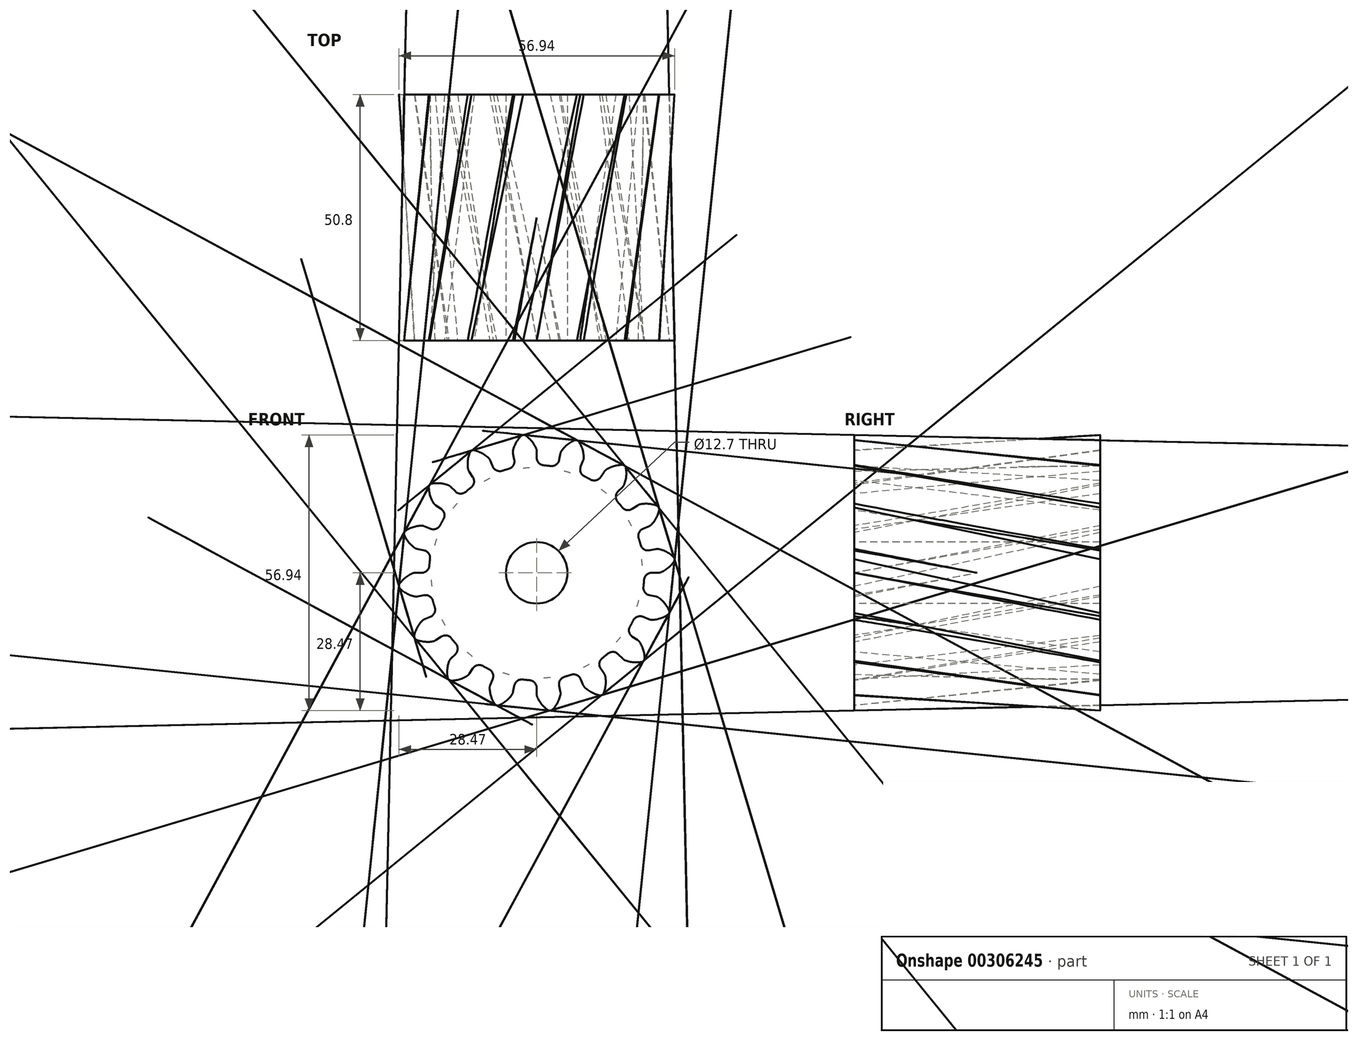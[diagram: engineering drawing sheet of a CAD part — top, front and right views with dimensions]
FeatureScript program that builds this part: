
annotation { "Feature Type Name" : "Feature", "Feature Type Description" : "" }
export const myFeature = defineFeature(function(context is Context, id is Id, definition is map)
    precondition{}
    {
        {
            var Q0;
            Q0=qCreatedBy(makeId("Front.planeOp"),FACE);
            var sketch = newSketch(context, id + "F0", { "sketchPlane" : qUnion([Q0])});
            skArc(sketch, "E0", {"start": v(-5.78, 21.46) * mm, "mid": v(-6.45, 21.27) * mm, "end": v(-7.12, 21.05) * mm});
            skArc(sketch, "E1.trimOffspring", {"start": v(-0.14, 25.74) * mm, "mid": v(-1.06, 27.2) * mm, "end": v(-2.34, 28.36) * mm});
            skLineSegment(sketch, "E2", {"start": v(-2.68, 28.45) * mm, "end": v(-2.8, 28.44) * mm});
            skLineSegment(sketch, "E3", {"start": v(0, 25.08) * mm, "end": v(0, 23.76) * mm});
            skLineSegment(sketch, "E4.MirrorCS", {"start": v(-4.9, 24.6) * mm, "end": v(-4.64, 23.3) * mm});
            skArc(sketch, "E5.MirrorCS", {"start": v(-4.88, 25.27) * mm, "mid": v(-4.27, 26.89) * mm, "end": v(-3.23, 28.28) * mm});
            skLineSegment(sketch, "E6.MirrorCS", {"start": v(-2.93, 28.43) * mm, "end": v(-2.8, 28.44) * mm});
            skPoint(sketch, "E7.visualSharp", {"position": v(-4.34, 21.8) * mm});
            skArc(sketch, "E7.filletArc", {"start": v(-5.78, 21.46) * mm, "mid": v(-4.84, 22.16) * mm, "end": v(-4.64, 23.3) * mm});
            skPoint(sketch, "E8.visualSharp", {"position": v(0, 22.23) * mm});
            skArc(sketch, "E8.filletArc", {"start": v(0, 23.76) * mm, "mid": v(0.43, 22.68) * mm, "end": v(1.48, 22.18) * mm});
            skPoint(sketch, "E9.visualSharp", {"position": v(-4.96, 24.91) * mm});
            skArc(sketch, "E9.filletArc", {"start": v(-4.88, 25.27) * mm, "mid": v(-4.92, 24.94) * mm, "end": v(-4.9, 24.6) * mm});
            skPoint(sketch, "E10.visualSharp", {"position": v(0, 25.4) * mm});
            skArc(sketch, "E10.filletArc", {"start": v(0, 25.08) * mm, "mid": v(-0.04, 25.42) * mm, "end": v(-0.14, 25.74) * mm});
            skPoint(sketch, "E11.visualSharp", {"position": v(-3.1, 28.4) * mm});
            skArc(sketch, "E11.filletArc", {"start": v(-2.93, 28.43) * mm, "mid": v(-3.1, 28.38) * mm, "end": v(-3.23, 28.28) * mm});
            skPoint(sketch, "E12.visualSharp", {"position": v(-2.5, 28.47) * mm});
            skArc(sketch, "E12.filletArc", {"start": v(-2.34, 28.36) * mm, "mid": v(-2.5, 28.44) * mm, "end": v(-2.68, 28.45) * mm});
            skPoint(sketch, "E13.1.0", {"position": v(-12.35, 18.48) * mm});
            skLineSegment(sketch, "E13.1.1", {"start": v(-9.6, 23.17) * mm, "end": v(-9.1, 21.95) * mm});
            skPoint(sketch, "E13.1.2", {"position": v(-13.2, 25.34) * mm});
            skArc(sketch, "E13.1.3", {"start": v(-14.18, 21.48) * mm, "mid": v(-14.23, 23.2) * mm, "end": v(-13.8, 24.89) * mm});
            skPoint(sketch, "E13.1.4", {"position": v(-13.74, 25.06) * mm});
            skPoint(sketch, "E13.1.5", {"position": v(-9.72, 23.47) * mm});
            skPoint(sketch, "E13.1.6", {"position": v(-14.11, 21.12) * mm});
            skPoint(sketch, "E13.1.7", {"position": v(-8.5, 20.53) * mm});
            skArc(sketch, "E13.1.8", {"start": v(-13.55, 17.62) * mm, "mid": v(-12.95, 18.62) * mm, "end": v(-13.2, 19.76) * mm});
            skArc(sketch, "E13.1.9", {"start": v(-9.98, 23.72) * mm, "mid": v(-11.4, 24.72) * mm, "end": v(-13.02, 25.3) * mm});
            skLineSegment(sketch, "E13.1.10", {"start": v(-13.94, 20.86) * mm, "end": v(-13.2, 19.76) * mm});
            skArc(sketch, "E13.1.11", {"start": v(-9.1, 21.95) * mm, "mid": v(-8.28, 21.11) * mm, "end": v(-7.12, 21.05) * mm});
            skArc(sketch, "E13.1.12", {"start": v(-14.18, 21.48) * mm, "mid": v(-14.1, 21.15) * mm, "end": v(-13.94, 20.86) * mm});
            skArc(sketch, "E13.1.13", {"start": v(-9.6, 23.17) * mm, "mid": v(-9.76, 23.47) * mm, "end": v(-9.98, 23.72) * mm});
            skArc(sketch, "E13.1.14", {"start": v(-13.58, 25.14) * mm, "mid": v(-13.72, 25.03) * mm, "end": v(-13.8, 24.89) * mm});
            skArc(sketch, "E13.1.15", {"start": v(-13.02, 25.3) * mm, "mid": v(-13.2, 25.31) * mm, "end": v(-13.36, 25.26) * mm});
            skLineSegment(sketch, "E13.1.16", {"start": v(-13.58, 25.14) * mm, "end": v(-13.47, 25.2) * mm});
            skLineSegment(sketch, "E13.1.17", {"start": v(-13.36, 25.26) * mm, "end": v(-13.47, 25.2) * mm});
            skPoint(sketch, "E13.2.0", {"position": v(-18.48, 12.35) * mm});
            skLineSegment(sketch, "E13.2.1", {"start": v(-17.74, 17.74) * mm, "end": v(-16.8, 16.8) * mm});
            skPoint(sketch, "E13.2.2", {"position": v(-21.9, 18.36) * mm});
            skArc(sketch, "E13.2.3", {"start": v(-21.32, 14.42) * mm, "mid": v(-22.03, 16) * mm, "end": v(-22.28, 17.7) * mm});
            skPoint(sketch, "E13.2.4", {"position": v(-22.28, 17.9) * mm});
            skPoint(sketch, "E13.2.5", {"position": v(-17.96, 17.96) * mm});
            skPoint(sketch, "E13.2.6", {"position": v(-21.12, 14.11) * mm});
            skPoint(sketch, "E13.2.7", {"position": v(-15.72, 15.72) * mm});
            skArc(sketch, "E13.2.8", {"start": v(-19.26, 11.09) * mm, "mid": v(-19.1, 12.24) * mm, "end": v(-19.76, 13.2) * mm});
            skArc(sketch, "E13.2.9", {"start": v(-18.3, 18.1) * mm, "mid": v(-19.99, 18.48) * mm, "end": v(-21.71, 18.4) * mm});
            skLineSegment(sketch, "E13.2.10", {"start": v(-20.86, 13.94) * mm, "end": v(-19.76, 13.2) * mm});
            skArc(sketch, "E13.2.11", {"start": v(-16.8, 16.8) * mm, "mid": v(-15.73, 16.34) * mm, "end": v(-14.63, 16.73) * mm});
            skArc(sketch, "E13.2.12", {"start": v(-21.32, 14.42) * mm, "mid": v(-21.11, 14.15) * mm, "end": v(-20.86, 13.94) * mm});
            skArc(sketch, "E13.2.13", {"start": v(-17.74, 17.74) * mm, "mid": v(-18, 17.95) * mm, "end": v(-18.3, 18.1) * mm});
            skArc(sketch, "E13.2.14", {"start": v(-22.17, 18.03) * mm, "mid": v(-22.25, 17.88) * mm, "end": v(-22.28, 17.7) * mm});
            skArc(sketch, "E13.2.15", {"start": v(-21.71, 18.4) * mm, "mid": v(-21.88, 18.34) * mm, "end": v(-22, 18.23) * mm});
            skLineSegment(sketch, "E13.2.16", {"start": v(-22.17, 18.03) * mm, "end": v(-22.1, 18.13) * mm});
            skLineSegment(sketch, "E13.2.17", {"start": v(-22, 18.23) * mm, "end": v(-22.1, 18.13) * mm});
            skLineSegment(sketch, "E14.1.3.0", {"start": v(-23.17, 9.6) * mm, "end": v(-21.95, 9.1) * mm});
            skPoint(sketch, "E14.4.3.0", {"position": v(-27.25, 8.59) * mm});
            skArc(sketch, "E14.5.3.0", {"start": v(-25.22, 5.16) * mm, "mid": v(-26.47, 6.35) * mm, "end": v(-27.36, 7.83) * mm});
            skPoint(sketch, "E14.9.3.0", {"position": v(-27.43, 8) * mm});
            skPoint(sketch, "E14.10.3.0", {"position": v(-23.47, 9.72) * mm});
            skPoint(sketch, "E14.11.3.0", {"position": v(-24.91, 4.96) * mm});
            skPoint(sketch, "E14.12.3.0", {"position": v(-20.53, 8.5) * mm});
            skArc(sketch, "E14.13.3.0", {"start": v(-22.04, 2.87) * mm, "mid": v(-22.32, 4) * mm, "end": v(-23.3, 4.64) * mm});
            skPoint(sketch, "E14.15.3.0", {"position": v(-21.8, 4.34) * mm});
            skArc(sketch, "E14.17.3.0", {"start": v(-23.83, 9.72) * mm, "mid": v(-25.54, 9.43) * mm, "end": v(-27.1, 8.69) * mm});
            skLineSegment(sketch, "E14.21.3.0", {"start": v(-24.6, 4.9) * mm, "end": v(-23.3, 4.64) * mm});
            skArc(sketch, "E14.24.3.0", {"start": v(-21.95, 9.1) * mm, "mid": v(-20.79, 9.07) * mm, "end": v(-19.92, 9.86) * mm});
            skArc(sketch, "E14.28.3.0", {"start": v(-25.22, 5.16) * mm, "mid": v(-24.92, 5) * mm, "end": v(-24.6, 4.9) * mm});
            skArc(sketch, "E14.32.3.0", {"start": v(-23.17, 9.6) * mm, "mid": v(-23.5, 9.7) * mm, "end": v(-23.83, 9.72) * mm});
            skArc(sketch, "E14.36.3.0", {"start": v(-27.38, 8.17) * mm, "mid": v(-27.4, 8) * mm, "end": v(-27.36, 7.83) * mm});
            skArc(sketch, "E14.40.3.0", {"start": v(-27.1, 8.69) * mm, "mid": v(-27.23, 8.57) * mm, "end": v(-27.3, 8.42) * mm});
            skLineSegment(sketch, "E14.44.3.0", {"start": v(-27.38, 8.17) * mm, "end": v(-27.35, 8.3) * mm});
            skLineSegment(sketch, "E14.47.3.0", {"start": v(-27.3, 8.42) * mm, "end": v(-27.35, 8.3) * mm});
            skLineSegment(sketch, "E14.1.4.0", {"start": v(-25.08, 0) * mm, "end": v(-23.76, 0) * mm});
            skPoint(sketch, "E14.4.4.0", {"position": v(-28.47, -2.5) * mm});
            skArc(sketch, "E14.5.4.0", {"start": v(-25.27, -4.88) * mm, "mid": v(-26.89, -4.27) * mm, "end": v(-28.28, -3.23) * mm});
            skPoint(sketch, "E14.9.4.0", {"position": v(-28.4, -3.1) * mm});
            skPoint(sketch, "E14.10.4.0", {"position": v(-25.4, 0) * mm});
            skPoint(sketch, "E14.11.4.0", {"position": v(-24.91, -4.96) * mm});
            skPoint(sketch, "E14.12.4.0", {"position": v(-22.23, 0) * mm});
            skArc(sketch, "E14.13.4.0", {"start": v(-21.46, -5.78) * mm, "mid": v(-22.16, -4.84) * mm, "end": v(-23.3, -4.64) * mm});
            skPoint(sketch, "E14.15.4.0", {"position": v(-21.8, -4.34) * mm});
            skArc(sketch, "E14.17.4.0", {"start": v(-25.74, -0.14) * mm, "mid": v(-27.2, -1.06) * mm, "end": v(-28.36, -2.34) * mm});
            skLineSegment(sketch, "E14.21.4.0", {"start": v(-24.6, -4.9) * mm, "end": v(-23.3, -4.64) * mm});
            skArc(sketch, "E14.24.4.0", {"start": v(-23.76, 0) * mm, "mid": v(-22.68, 0.43) * mm, "end": v(-22.18, 1.48) * mm});
            skArc(sketch, "E14.28.4.0", {"start": v(-25.27, -4.88) * mm, "mid": v(-24.94, -4.92) * mm, "end": v(-24.6, -4.9) * mm});
            skArc(sketch, "E14.32.4.0", {"start": v(-25.08, 0) * mm, "mid": v(-25.42, -0.04) * mm, "end": v(-25.74, -0.14) * mm});
            skArc(sketch, "E14.36.4.0", {"start": v(-28.43, -2.93) * mm, "mid": v(-28.38, -3.1) * mm, "end": v(-28.28, -3.23) * mm});
            skArc(sketch, "E14.40.4.0", {"start": v(-28.36, -2.34) * mm, "mid": v(-28.44, -2.5) * mm, "end": v(-28.45, -2.68) * mm});
            skLineSegment(sketch, "E14.44.4.0", {"start": v(-28.43, -2.93) * mm, "end": v(-28.44, -2.8) * mm});
            skLineSegment(sketch, "E14.47.4.0", {"start": v(-28.45, -2.68) * mm, "end": v(-28.44, -2.8) * mm});
            skLineSegment(sketch, "E14.1.5.0", {"start": v(-23.17, -9.6) * mm, "end": v(-21.95, -9.1) * mm});
            skPoint(sketch, "E14.4.5.0", {"position": v(-25.34, -13.2) * mm});
            skArc(sketch, "E14.5.5.0", {"start": v(-21.48, -14.18) * mm, "mid": v(-23.2, -14.23) * mm, "end": v(-24.89, -13.8) * mm});
            skPoint(sketch, "E14.9.5.0", {"position": v(-25.06, -13.74) * mm});
            skPoint(sketch, "E14.10.5.0", {"position": v(-23.47, -9.72) * mm});
            skPoint(sketch, "E14.11.5.0", {"position": v(-21.12, -14.11) * mm});
            skPoint(sketch, "E14.12.5.0", {"position": v(-20.53, -8.5) * mm});
            skArc(sketch, "E14.13.5.0", {"start": v(-17.62, -13.55) * mm, "mid": v(-18.62, -12.95) * mm, "end": v(-19.76, -13.2) * mm});
            skPoint(sketch, "E14.15.5.0", {"position": v(-18.48, -12.35) * mm});
            skArc(sketch, "E14.17.5.0", {"start": v(-23.72, -9.98) * mm, "mid": v(-24.72, -11.4) * mm, "end": v(-25.3, -13.02) * mm});
            skLineSegment(sketch, "E14.21.5.0", {"start": v(-20.86, -13.94) * mm, "end": v(-19.76, -13.2) * mm});
            skArc(sketch, "E14.24.5.0", {"start": v(-21.95, -9.1) * mm, "mid": v(-21.11, -8.28) * mm, "end": v(-21.05, -7.12) * mm});
            skArc(sketch, "E14.28.5.0", {"start": v(-21.48, -14.18) * mm, "mid": v(-21.15, -14.1) * mm, "end": v(-20.86, -13.94) * mm});
            skArc(sketch, "E14.32.5.0", {"start": v(-23.17, -9.6) * mm, "mid": v(-23.47, -9.76) * mm, "end": v(-23.72, -9.98) * mm});
            skArc(sketch, "E14.36.5.0", {"start": v(-25.14, -13.58) * mm, "mid": v(-25.03, -13.72) * mm, "end": v(-24.89, -13.8) * mm});
            skArc(sketch, "E14.40.5.0", {"start": v(-25.3, -13.02) * mm, "mid": v(-25.31, -13.2) * mm, "end": v(-25.26, -13.36) * mm});
            skLineSegment(sketch, "E14.44.5.0", {"start": v(-25.14, -13.58) * mm, "end": v(-25.2, -13.47) * mm});
            skLineSegment(sketch, "E14.47.5.0", {"start": v(-25.26, -13.36) * mm, "end": v(-25.2, -13.47) * mm});
            skLineSegment(sketch, "E14.1.6.0", {"start": v(-17.74, -17.74) * mm, "end": v(-16.8, -16.8) * mm});
            skPoint(sketch, "E14.4.6.0", {"position": v(-18.36, -21.9) * mm});
            skArc(sketch, "E14.5.6.0", {"start": v(-14.42, -21.32) * mm, "mid": v(-16, -22.03) * mm, "end": v(-17.7, -22.28) * mm});
            skPoint(sketch, "E14.9.6.0", {"position": v(-17.9, -22.28) * mm});
            skPoint(sketch, "E14.10.6.0", {"position": v(-17.96, -17.96) * mm});
            skPoint(sketch, "E14.11.6.0", {"position": v(-14.11, -21.12) * mm});
            skPoint(sketch, "E14.12.6.0", {"position": v(-15.72, -15.72) * mm});
            skArc(sketch, "E14.13.6.0", {"start": v(-11.09, -19.26) * mm, "mid": v(-12.24, -19.1) * mm, "end": v(-13.2, -19.76) * mm});
            skPoint(sketch, "E14.15.6.0", {"position": v(-12.35, -18.48) * mm});
            skArc(sketch, "E14.17.6.0", {"start": v(-18.1, -18.3) * mm, "mid": v(-18.48, -19.99) * mm, "end": v(-18.4, -21.71) * mm});
            skLineSegment(sketch, "E14.21.6.0", {"start": v(-13.94, -20.86) * mm, "end": v(-13.2, -19.76) * mm});
            skArc(sketch, "E14.24.6.0", {"start": v(-16.8, -16.8) * mm, "mid": v(-16.34, -15.73) * mm, "end": v(-16.73, -14.63) * mm});
            skArc(sketch, "E14.28.6.0", {"start": v(-14.42, -21.32) * mm, "mid": v(-14.15, -21.11) * mm, "end": v(-13.94, -20.86) * mm});
            skArc(sketch, "E14.32.6.0", {"start": v(-17.74, -17.74) * mm, "mid": v(-17.95, -18) * mm, "end": v(-18.1, -18.3) * mm});
            skArc(sketch, "E14.36.6.0", {"start": v(-18.03, -22.17) * mm, "mid": v(-17.88, -22.25) * mm, "end": v(-17.7, -22.28) * mm});
            skArc(sketch, "E14.40.6.0", {"start": v(-18.4, -21.71) * mm, "mid": v(-18.34, -21.88) * mm, "end": v(-18.23, -22) * mm});
            skLineSegment(sketch, "E14.44.6.0", {"start": v(-18.03, -22.17) * mm, "end": v(-18.13, -22.1) * mm});
            skLineSegment(sketch, "E14.47.6.0", {"start": v(-18.23, -22) * mm, "end": v(-18.13, -22.1) * mm});
            skLineSegment(sketch, "E14.1.7.0", {"start": v(-9.6, -23.17) * mm, "end": v(-9.1, -21.95) * mm});
            skPoint(sketch, "E14.4.7.0", {"position": v(-8.59, -27.25) * mm});
            skArc(sketch, "E14.5.7.0", {"start": v(-5.16, -25.22) * mm, "mid": v(-6.35, -26.47) * mm, "end": v(-7.83, -27.36) * mm});
            skPoint(sketch, "E14.9.7.0", {"position": v(-8, -27.43) * mm});
            skPoint(sketch, "E14.10.7.0", {"position": v(-9.72, -23.47) * mm});
            skPoint(sketch, "E14.11.7.0", {"position": v(-4.96, -24.91) * mm});
            skPoint(sketch, "E14.12.7.0", {"position": v(-8.5, -20.53) * mm});
            skArc(sketch, "E14.13.7.0", {"start": v(-2.87, -22.04) * mm, "mid": v(-4, -22.32) * mm, "end": v(-4.64, -23.3) * mm});
            skPoint(sketch, "E14.15.7.0", {"position": v(-4.34, -21.8) * mm});
            skArc(sketch, "E14.17.7.0", {"start": v(-9.72, -23.83) * mm, "mid": v(-9.43, -25.54) * mm, "end": v(-8.69, -27.1) * mm});
            skLineSegment(sketch, "E14.21.7.0", {"start": v(-4.9, -24.6) * mm, "end": v(-4.64, -23.3) * mm});
            skArc(sketch, "E14.24.7.0", {"start": v(-9.1, -21.95) * mm, "mid": v(-9.07, -20.79) * mm, "end": v(-9.86, -19.92) * mm});
            skArc(sketch, "E14.28.7.0", {"start": v(-5.16, -25.22) * mm, "mid": v(-5, -24.92) * mm, "end": v(-4.9, -24.6) * mm});
            skArc(sketch, "E14.32.7.0", {"start": v(-9.6, -23.17) * mm, "mid": v(-9.7, -23.5) * mm, "end": v(-9.72, -23.83) * mm});
            skArc(sketch, "E14.36.7.0", {"start": v(-8.17, -27.38) * mm, "mid": v(-8, -27.4) * mm, "end": v(-7.83, -27.36) * mm});
            skArc(sketch, "E14.40.7.0", {"start": v(-8.69, -27.1) * mm, "mid": v(-8.57, -27.23) * mm, "end": v(-8.42, -27.3) * mm});
            skLineSegment(sketch, "E14.44.7.0", {"start": v(-8.17, -27.38) * mm, "end": v(-8.3, -27.35) * mm});
            skLineSegment(sketch, "E14.47.7.0", {"start": v(-8.42, -27.3) * mm, "end": v(-8.3, -27.35) * mm});
            skLineSegment(sketch, "E14.1.8.0", {"start": v(0, -25.08) * mm, "end": v(0, -23.76) * mm});
            skPoint(sketch, "E14.4.8.0", {"position": v(2.5, -28.47) * mm});
            skArc(sketch, "E14.5.8.0", {"start": v(4.88, -25.27) * mm, "mid": v(4.27, -26.89) * mm, "end": v(3.23, -28.28) * mm});
            skPoint(sketch, "E14.9.8.0", {"position": v(3.1, -28.4) * mm});
            skPoint(sketch, "E14.10.8.0", {"position": v(0, -25.4) * mm});
            skPoint(sketch, "E14.11.8.0", {"position": v(4.96, -24.91) * mm});
            skPoint(sketch, "E14.12.8.0", {"position": v(0, -22.23) * mm});
            skArc(sketch, "E14.13.8.0", {"start": v(5.78, -21.46) * mm, "mid": v(4.84, -22.16) * mm, "end": v(4.64, -23.3) * mm});
            skPoint(sketch, "E14.15.8.0", {"position": v(4.34, -21.8) * mm});
            skArc(sketch, "E14.17.8.0", {"start": v(0.14, -25.74) * mm, "mid": v(1.06, -27.2) * mm, "end": v(2.34, -28.36) * mm});
            skLineSegment(sketch, "E14.21.8.0", {"start": v(4.9, -24.6) * mm, "end": v(4.64, -23.3) * mm});
            skArc(sketch, "E14.24.8.0", {"start": v(0, -23.76) * mm, "mid": v(-0.43, -22.68) * mm, "end": v(-1.48, -22.18) * mm});
            skArc(sketch, "E14.28.8.0", {"start": v(4.88, -25.27) * mm, "mid": v(4.92, -24.94) * mm, "end": v(4.9, -24.6) * mm});
            skArc(sketch, "E14.32.8.0", {"start": v(0, -25.08) * mm, "mid": v(0.04, -25.42) * mm, "end": v(0.14, -25.74) * mm});
            skArc(sketch, "E14.36.8.0", {"start": v(2.93, -28.43) * mm, "mid": v(3.1, -28.38) * mm, "end": v(3.23, -28.28) * mm});
            skArc(sketch, "E14.40.8.0", {"start": v(2.34, -28.36) * mm, "mid": v(2.5, -28.44) * mm, "end": v(2.68, -28.45) * mm});
            skLineSegment(sketch, "E14.44.8.0", {"start": v(2.93, -28.43) * mm, "end": v(2.8, -28.44) * mm});
            skLineSegment(sketch, "E14.47.8.0", {"start": v(2.68, -28.45) * mm, "end": v(2.8, -28.44) * mm});
            skLineSegment(sketch, "E14.1.9.0", {"start": v(9.6, -23.17) * mm, "end": v(9.1, -21.95) * mm});
            skPoint(sketch, "E14.4.9.0", {"position": v(13.2, -25.34) * mm});
            skArc(sketch, "E14.5.9.0", {"start": v(14.18, -21.48) * mm, "mid": v(14.23, -23.2) * mm, "end": v(13.8, -24.89) * mm});
            skPoint(sketch, "E14.9.9.0", {"position": v(13.74, -25.06) * mm});
            skPoint(sketch, "E14.10.9.0", {"position": v(9.72, -23.47) * mm});
            skPoint(sketch, "E14.11.9.0", {"position": v(14.11, -21.12) * mm});
            skPoint(sketch, "E14.12.9.0", {"position": v(8.5, -20.53) * mm});
            skArc(sketch, "E14.13.9.0", {"start": v(13.55, -17.62) * mm, "mid": v(12.95, -18.62) * mm, "end": v(13.2, -19.76) * mm});
            skPoint(sketch, "E14.15.9.0", {"position": v(12.35, -18.48) * mm});
            skArc(sketch, "E14.17.9.0", {"start": v(9.98, -23.72) * mm, "mid": v(11.4, -24.72) * mm, "end": v(13.02, -25.3) * mm});
            skLineSegment(sketch, "E14.21.9.0", {"start": v(13.94, -20.86) * mm, "end": v(13.2, -19.76) * mm});
            skArc(sketch, "E14.24.9.0", {"start": v(9.1, -21.95) * mm, "mid": v(8.28, -21.11) * mm, "end": v(7.12, -21.05) * mm});
            skArc(sketch, "E14.28.9.0", {"start": v(14.18, -21.48) * mm, "mid": v(14.1, -21.15) * mm, "end": v(13.94, -20.86) * mm});
            skArc(sketch, "E14.32.9.0", {"start": v(9.6, -23.17) * mm, "mid": v(9.76, -23.47) * mm, "end": v(9.98, -23.72) * mm});
            skArc(sketch, "E14.36.9.0", {"start": v(13.58, -25.14) * mm, "mid": v(13.72, -25.03) * mm, "end": v(13.8, -24.89) * mm});
            skArc(sketch, "E14.40.9.0", {"start": v(13.02, -25.3) * mm, "mid": v(13.2, -25.31) * mm, "end": v(13.36, -25.26) * mm});
            skLineSegment(sketch, "E14.44.9.0", {"start": v(13.58, -25.14) * mm, "end": v(13.47, -25.2) * mm});
            skLineSegment(sketch, "E14.47.9.0", {"start": v(13.36, -25.26) * mm, "end": v(13.47, -25.2) * mm});
            skLineSegment(sketch, "E14.1.10.0", {"start": v(17.74, -17.74) * mm, "end": v(16.8, -16.8) * mm});
            skPoint(sketch, "E14.4.10.0", {"position": v(21.9, -18.36) * mm});
            skArc(sketch, "E14.5.10.0", {"start": v(21.32, -14.42) * mm, "mid": v(22.03, -16) * mm, "end": v(22.28, -17.7) * mm});
            skPoint(sketch, "E14.9.10.0", {"position": v(22.28, -17.9) * mm});
            skPoint(sketch, "E14.10.10.0", {"position": v(17.96, -17.96) * mm});
            skPoint(sketch, "E14.11.10.0", {"position": v(21.12, -14.11) * mm});
            skPoint(sketch, "E14.12.10.0", {"position": v(15.72, -15.72) * mm});
            skArc(sketch, "E14.13.10.0", {"start": v(19.26, -11.09) * mm, "mid": v(19.1, -12.24) * mm, "end": v(19.76, -13.2) * mm});
            skPoint(sketch, "E14.15.10.0", {"position": v(18.48, -12.35) * mm});
            skArc(sketch, "E14.17.10.0", {"start": v(18.3, -18.1) * mm, "mid": v(19.99, -18.48) * mm, "end": v(21.71, -18.4) * mm});
            skLineSegment(sketch, "E14.21.10.0", {"start": v(20.86, -13.94) * mm, "end": v(19.76, -13.2) * mm});
            skArc(sketch, "E14.24.10.0", {"start": v(16.8, -16.8) * mm, "mid": v(15.73, -16.34) * mm, "end": v(14.63, -16.73) * mm});
            skArc(sketch, "E14.28.10.0", {"start": v(21.32, -14.42) * mm, "mid": v(21.11, -14.15) * mm, "end": v(20.86, -13.94) * mm});
            skArc(sketch, "E14.32.10.0", {"start": v(17.74, -17.74) * mm, "mid": v(18, -17.95) * mm, "end": v(18.3, -18.1) * mm});
            skArc(sketch, "E14.36.10.0", {"start": v(22.17, -18.03) * mm, "mid": v(22.25, -17.88) * mm, "end": v(22.28, -17.7) * mm});
            skArc(sketch, "E14.40.10.0", {"start": v(21.71, -18.4) * mm, "mid": v(21.88, -18.34) * mm, "end": v(22, -18.23) * mm});
            skLineSegment(sketch, "E14.44.10.0", {"start": v(22.17, -18.03) * mm, "end": v(22.1, -18.13) * mm});
            skLineSegment(sketch, "E14.47.10.0", {"start": v(22, -18.23) * mm, "end": v(22.1, -18.13) * mm});
            skLineSegment(sketch, "E14.1.11.0", {"start": v(23.17, -9.6) * mm, "end": v(21.95, -9.1) * mm});
            skPoint(sketch, "E14.4.11.0", {"position": v(27.25, -8.59) * mm});
            skArc(sketch, "E14.5.11.0", {"start": v(25.22, -5.16) * mm, "mid": v(26.47, -6.35) * mm, "end": v(27.36, -7.83) * mm});
            skPoint(sketch, "E14.9.11.0", {"position": v(27.43, -8) * mm});
            skPoint(sketch, "E14.10.11.0", {"position": v(23.47, -9.72) * mm});
            skPoint(sketch, "E14.11.11.0", {"position": v(24.91, -4.96) * mm});
            skPoint(sketch, "E14.12.11.0", {"position": v(20.53, -8.5) * mm});
            skArc(sketch, "E14.13.11.0", {"start": v(22.04, -2.87) * mm, "mid": v(22.32, -4) * mm, "end": v(23.3, -4.64) * mm});
            skPoint(sketch, "E14.15.11.0", {"position": v(21.8, -4.34) * mm});
            skArc(sketch, "E14.17.11.0", {"start": v(23.83, -9.72) * mm, "mid": v(25.54, -9.43) * mm, "end": v(27.1, -8.69) * mm});
            skLineSegment(sketch, "E14.21.11.0", {"start": v(24.6, -4.9) * mm, "end": v(23.3, -4.64) * mm});
            skArc(sketch, "E14.24.11.0", {"start": v(21.95, -9.1) * mm, "mid": v(20.79, -9.07) * mm, "end": v(19.92, -9.86) * mm});
            skArc(sketch, "E14.28.11.0", {"start": v(25.22, -5.16) * mm, "mid": v(24.92, -5) * mm, "end": v(24.6, -4.9) * mm});
            skArc(sketch, "E14.32.11.0", {"start": v(23.17, -9.6) * mm, "mid": v(23.5, -9.7) * mm, "end": v(23.83, -9.72) * mm});
            skArc(sketch, "E14.36.11.0", {"start": v(27.38, -8.17) * mm, "mid": v(27.4, -8) * mm, "end": v(27.36, -7.83) * mm});
            skArc(sketch, "E14.40.11.0", {"start": v(27.1, -8.69) * mm, "mid": v(27.23, -8.57) * mm, "end": v(27.3, -8.42) * mm});
            skLineSegment(sketch, "E14.44.11.0", {"start": v(27.38, -8.17) * mm, "end": v(27.35, -8.3) * mm});
            skLineSegment(sketch, "E14.47.11.0", {"start": v(27.3, -8.42) * mm, "end": v(27.35, -8.3) * mm});
            skLineSegment(sketch, "E14.1.12.0", {"start": v(25.08, 0) * mm, "end": v(23.76, 0) * mm});
            skPoint(sketch, "E14.4.12.0", {"position": v(28.47, 2.5) * mm});
            skArc(sketch, "E14.5.12.0", {"start": v(25.27, 4.88) * mm, "mid": v(26.89, 4.27) * mm, "end": v(28.28, 3.23) * mm});
            skPoint(sketch, "E14.9.12.0", {"position": v(28.4, 3.1) * mm});
            skPoint(sketch, "E14.10.12.0", {"position": v(25.4, 0) * mm});
            skPoint(sketch, "E14.11.12.0", {"position": v(24.91, 4.96) * mm});
            skPoint(sketch, "E14.12.12.0", {"position": v(22.23, 0) * mm});
            skArc(sketch, "E14.13.12.0", {"start": v(21.46, 5.78) * mm, "mid": v(22.16, 4.84) * mm, "end": v(23.3, 4.64) * mm});
            skPoint(sketch, "E14.15.12.0", {"position": v(21.8, 4.34) * mm});
            skArc(sketch, "E14.17.12.0", {"start": v(25.74, 0.14) * mm, "mid": v(27.2, 1.06) * mm, "end": v(28.36, 2.34) * mm});
            skLineSegment(sketch, "E14.21.12.0", {"start": v(24.6, 4.9) * mm, "end": v(23.3, 4.64) * mm});
            skArc(sketch, "E14.24.12.0", {"start": v(23.76, 0) * mm, "mid": v(22.68, -0.43) * mm, "end": v(22.18, -1.48) * mm});
            skArc(sketch, "E14.28.12.0", {"start": v(25.27, 4.88) * mm, "mid": v(24.94, 4.92) * mm, "end": v(24.6, 4.9) * mm});
            skArc(sketch, "E14.32.12.0", {"start": v(25.08, 0) * mm, "mid": v(25.42, 0.04) * mm, "end": v(25.74, 0.14) * mm});
            skArc(sketch, "E14.36.12.0", {"start": v(28.43, 2.93) * mm, "mid": v(28.38, 3.1) * mm, "end": v(28.28, 3.23) * mm});
            skArc(sketch, "E14.40.12.0", {"start": v(28.36, 2.34) * mm, "mid": v(28.44, 2.5) * mm, "end": v(28.45, 2.68) * mm});
            skLineSegment(sketch, "E14.44.12.0", {"start": v(28.43, 2.93) * mm, "end": v(28.44, 2.8) * mm});
            skLineSegment(sketch, "E14.47.12.0", {"start": v(28.45, 2.68) * mm, "end": v(28.44, 2.8) * mm});
            skLineSegment(sketch, "E14.1.13.0", {"start": v(23.17, 9.6) * mm, "end": v(21.95, 9.1) * mm});
            skPoint(sketch, "E14.4.13.0", {"position": v(25.34, 13.2) * mm});
            skArc(sketch, "E14.5.13.0", {"start": v(21.48, 14.18) * mm, "mid": v(23.2, 14.23) * mm, "end": v(24.89, 13.8) * mm});
            skPoint(sketch, "E14.9.13.0", {"position": v(25.06, 13.74) * mm});
            skPoint(sketch, "E14.10.13.0", {"position": v(23.47, 9.72) * mm});
            skPoint(sketch, "E14.11.13.0", {"position": v(21.12, 14.11) * mm});
            skPoint(sketch, "E14.12.13.0", {"position": v(20.53, 8.5) * mm});
            skArc(sketch, "E14.13.13.0", {"start": v(17.62, 13.55) * mm, "mid": v(18.62, 12.95) * mm, "end": v(19.76, 13.2) * mm});
            skPoint(sketch, "E14.15.13.0", {"position": v(18.48, 12.35) * mm});
            skArc(sketch, "E14.17.13.0", {"start": v(23.72, 9.98) * mm, "mid": v(24.72, 11.4) * mm, "end": v(25.3, 13.02) * mm});
            skLineSegment(sketch, "E14.21.13.0", {"start": v(20.86, 13.94) * mm, "end": v(19.76, 13.2) * mm});
            skArc(sketch, "E14.24.13.0", {"start": v(21.95, 9.1) * mm, "mid": v(21.11, 8.28) * mm, "end": v(21.05, 7.12) * mm});
            skArc(sketch, "E14.28.13.0", {"start": v(21.48, 14.18) * mm, "mid": v(21.15, 14.1) * mm, "end": v(20.86, 13.94) * mm});
            skArc(sketch, "E14.32.13.0", {"start": v(23.17, 9.6) * mm, "mid": v(23.47, 9.76) * mm, "end": v(23.72, 9.98) * mm});
            skArc(sketch, "E14.36.13.0", {"start": v(25.14, 13.58) * mm, "mid": v(25.03, 13.72) * mm, "end": v(24.89, 13.8) * mm});
            skArc(sketch, "E14.40.13.0", {"start": v(25.3, 13.02) * mm, "mid": v(25.31, 13.2) * mm, "end": v(25.26, 13.36) * mm});
            skLineSegment(sketch, "E14.44.13.0", {"start": v(25.14, 13.58) * mm, "end": v(25.2, 13.47) * mm});
            skLineSegment(sketch, "E14.47.13.0", {"start": v(25.26, 13.36) * mm, "end": v(25.2, 13.47) * mm});
            skLineSegment(sketch, "E14.1.14.0", {"start": v(17.74, 17.74) * mm, "end": v(16.8, 16.8) * mm});
            skPoint(sketch, "E14.4.14.0", {"position": v(18.36, 21.9) * mm});
            skArc(sketch, "E14.5.14.0", {"start": v(14.42, 21.32) * mm, "mid": v(16, 22.03) * mm, "end": v(17.7, 22.28) * mm});
            skPoint(sketch, "E14.9.14.0", {"position": v(17.9, 22.28) * mm});
            skPoint(sketch, "E14.10.14.0", {"position": v(17.96, 17.96) * mm});
            skPoint(sketch, "E14.11.14.0", {"position": v(14.11, 21.12) * mm});
            skPoint(sketch, "E14.12.14.0", {"position": v(15.72, 15.72) * mm});
            skArc(sketch, "E14.13.14.0", {"start": v(11.09, 19.26) * mm, "mid": v(12.24, 19.1) * mm, "end": v(13.2, 19.76) * mm});
            skPoint(sketch, "E14.15.14.0", {"position": v(12.35, 18.48) * mm});
            skArc(sketch, "E14.17.14.0", {"start": v(18.1, 18.3) * mm, "mid": v(18.48, 19.99) * mm, "end": v(18.4, 21.71) * mm});
            skLineSegment(sketch, "E14.21.14.0", {"start": v(13.94, 20.86) * mm, "end": v(13.2, 19.76) * mm});
            skArc(sketch, "E14.24.14.0", {"start": v(16.8, 16.8) * mm, "mid": v(16.34, 15.73) * mm, "end": v(16.73, 14.63) * mm});
            skArc(sketch, "E14.28.14.0", {"start": v(14.42, 21.32) * mm, "mid": v(14.15, 21.11) * mm, "end": v(13.94, 20.86) * mm});
            skArc(sketch, "E14.32.14.0", {"start": v(17.74, 17.74) * mm, "mid": v(17.95, 18) * mm, "end": v(18.1, 18.3) * mm});
            skArc(sketch, "E14.36.14.0", {"start": v(18.03, 22.17) * mm, "mid": v(17.88, 22.25) * mm, "end": v(17.7, 22.28) * mm});
            skArc(sketch, "E14.40.14.0", {"start": v(18.4, 21.71) * mm, "mid": v(18.34, 21.88) * mm, "end": v(18.23, 22) * mm});
            skLineSegment(sketch, "E14.44.14.0", {"start": v(18.03, 22.17) * mm, "end": v(18.13, 22.1) * mm});
            skLineSegment(sketch, "E14.47.14.0", {"start": v(18.23, 22) * mm, "end": v(18.13, 22.1) * mm});
            skLineSegment(sketch, "E14.1.15.0", {"start": v(9.6, 23.17) * mm, "end": v(9.1, 21.95) * mm});
            skPoint(sketch, "E14.4.15.0", {"position": v(8.59, 27.25) * mm});
            skArc(sketch, "E14.5.15.0", {"start": v(5.16, 25.22) * mm, "mid": v(6.35, 26.47) * mm, "end": v(7.83, 27.36) * mm});
            skPoint(sketch, "E14.9.15.0", {"position": v(8, 27.43) * mm});
            skPoint(sketch, "E14.10.15.0", {"position": v(9.72, 23.47) * mm});
            skPoint(sketch, "E14.11.15.0", {"position": v(4.96, 24.91) * mm});
            skPoint(sketch, "E14.12.15.0", {"position": v(8.5, 20.53) * mm});
            skArc(sketch, "E14.13.15.0", {"start": v(2.87, 22.04) * mm, "mid": v(4, 22.32) * mm, "end": v(4.64, 23.3) * mm});
            skPoint(sketch, "E14.15.15.0", {"position": v(4.34, 21.8) * mm});
            skArc(sketch, "E14.17.15.0", {"start": v(9.72, 23.83) * mm, "mid": v(9.43, 25.54) * mm, "end": v(8.69, 27.1) * mm});
            skLineSegment(sketch, "E14.21.15.0", {"start": v(4.9, 24.6) * mm, "end": v(4.64, 23.3) * mm});
            skArc(sketch, "E14.24.15.0", {"start": v(9.1, 21.95) * mm, "mid": v(9.07, 20.79) * mm, "end": v(9.86, 19.92) * mm});
            skArc(sketch, "E14.28.15.0", {"start": v(5.16, 25.22) * mm, "mid": v(5, 24.92) * mm, "end": v(4.9, 24.6) * mm});
            skArc(sketch, "E14.32.15.0", {"start": v(9.6, 23.17) * mm, "mid": v(9.7, 23.5) * mm, "end": v(9.72, 23.83) * mm});
            skArc(sketch, "E14.36.15.0", {"start": v(8.17, 27.38) * mm, "mid": v(8, 27.4) * mm, "end": v(7.83, 27.36) * mm});
            skArc(sketch, "E14.40.15.0", {"start": v(8.69, 27.1) * mm, "mid": v(8.57, 27.23) * mm, "end": v(8.42, 27.3) * mm});
            skLineSegment(sketch, "E14.44.15.0", {"start": v(8.17, 27.38) * mm, "end": v(8.3, 27.35) * mm});
            skLineSegment(sketch, "E14.47.15.0", {"start": v(8.42, 27.3) * mm, "end": v(8.3, 27.35) * mm});
            skArc(sketch, "E15.trimOffspring", {"start": v(2.87, 22.04) * mm, "mid": v(2.18, 22.12) * mm, "end": v(1.48, 22.18) * mm});
            skArc(sketch, "E16.trimOffspring", {"start": v(12.35, 18.48) * mm, "mid": v(11.12, 19.24) * mm, "end": v(9.86, 19.92) * mm});
            skArc(sketch, "E17.trimOffspring", {"start": v(17.62, 13.55) * mm, "mid": v(17.18, 14.1) * mm, "end": v(16.73, 14.63) * mm});
            skArc(sketch, "E18.trimOffspring", {"start": v(21.46, 5.78) * mm, "mid": v(21.27, 6.45) * mm, "end": v(21.05, 7.12) * mm});
            skArc(sketch, "E19.trimOffspring", {"start": v(22.04, -2.87) * mm, "mid": v(22.12, -2.18) * mm, "end": v(22.18, -1.48) * mm});
            skArc(sketch, "E20.trimOffspring", {"start": v(19.26, -11.09) * mm, "mid": v(19.6, -10.48) * mm, "end": v(19.92, -9.86) * mm});
            skArc(sketch, "E21.trimOffspring", {"start": v(13.55, -17.62) * mm, "mid": v(14.1, -17.18) * mm, "end": v(14.63, -16.73) * mm});
            skArc(sketch, "E22.trimOffspring", {"start": v(5.78, -21.46) * mm, "mid": v(6.45, -21.27) * mm, "end": v(7.12, -21.05) * mm});
            skArc(sketch, "E23.trimOffspring", {"start": v(-2.87, -22.04) * mm, "mid": v(-2.18, -22.12) * mm, "end": v(-1.48, -22.18) * mm});
            skArc(sketch, "E24.trimOffspring", {"start": v(-11.09, -19.26) * mm, "mid": v(-10.48, -19.6) * mm, "end": v(-9.86, -19.92) * mm});
            skArc(sketch, "E25.trimOffspring", {"start": v(-17.62, -13.55) * mm, "mid": v(-17.18, -14.1) * mm, "end": v(-16.73, -14.63) * mm});
            skArc(sketch, "E26.trimOffspring", {"start": v(-21.46, -5.78) * mm, "mid": v(-21.27, -6.45) * mm, "end": v(-21.05, -7.12) * mm});
            skArc(sketch, "E27.trimOffspring", {"start": v(-22.04, 2.87) * mm, "mid": v(-22.12, 2.18) * mm, "end": v(-22.18, 1.48) * mm});
            skArc(sketch, "E28.trimOffspring", {"start": v(-19.26, 11.09) * mm, "mid": v(-19.6, 10.48) * mm, "end": v(-19.92, 9.86) * mm});
            skArc(sketch, "E29.trimOffspring", {"start": v(-13.55, 17.62) * mm, "mid": v(-14.1, 17.18) * mm, "end": v(-14.63, 16.73) * mm});
            skSolve(sketch);
        }
        {
            var Q0;
            Q0=qCreatedBy(makeId("Front.planeOp"),FACE);
            cPlane(context, id + "F1", {"entities" : qUnion([Q0]), "cplaneType" : CPlaneType.OFFSET, "offset" : 50.8 * mm, "width" : 152.4 * mm, "height" : 152.4 * mm});
        }
        {
            var Q0;
            Q0=qCreatedBy(id+"F1.planeOp",FACE);
            var sketch = newSketch(context, id + "F2", { "sketchPlane" : qUnion([Q0])});
            skArc(sketch, "E30", {"start": v(-5.78, 21.46) * mm, "mid": v(-6.45, 21.27) * mm, "end": v(-7.12, 21.05) * mm});
            skArc(sketch, "E31.trimOffspring", {"start": v(-0.14, 25.74) * mm, "mid": v(-1.07, 27.21) * mm, "end": v(-2.37, 28.38) * mm});
            skLineSegment(sketch, "E32", {"start": v(-2.65, 28.47) * mm, "end": v(-2.8, 28.47) * mm});
            skLineSegment(sketch, "E33", {"start": v(0, 25.08) * mm, "end": v(0, 23.76) * mm});
            skLineSegment(sketch, "E34.MirrorCS", {"start": v(-2.95, 28.44) * mm, "end": v(-2.8, 28.47) * mm});
            skArc(sketch, "E35.MirrorCS", {"start": v(-4.88, 25.27) * mm, "mid": v(-4.26, 26.9) * mm, "end": v(-3.22, 28.3) * mm});
            skLineSegment(sketch, "E36.MirrorCS", {"start": v(-4.9, 24.6) * mm, "end": v(-4.64, 23.3) * mm});
            skPoint(sketch, "E37.visualSharp", {"position": v(-4.34, 21.8) * mm});
            skArc(sketch, "E37.filletArc", {"start": v(-4.7, 21.72) * mm, "mid": v(-4.46, 21.88) * mm, "end": v(-4.4, 22.16) * mm});
            skArc(sketch, "E38.filletArc", {"start": v(-5.78, 21.46) * mm, "mid": v(-4.84, 22.16) * mm, "end": v(-4.64, 23.3) * mm});
            skPoint(sketch, "E39.visualSharp", {"position": v(0, 22.23) * mm});
            skArc(sketch, "E39.filletArc", {"start": v(0, 23.76) * mm, "mid": v(0.43, 22.68) * mm, "end": v(1.48, 22.18) * mm});
            skPoint(sketch, "E40.visualSharp", {"position": v(-4.96, 24.91) * mm});
            skArc(sketch, "E40.filletArc", {"start": v(-4.88, 25.27) * mm, "mid": v(-4.92, 24.94) * mm, "end": v(-4.9, 24.6) * mm});
            skPoint(sketch, "E41.visualSharp", {"position": v(0, 25.4) * mm});
            skArc(sketch, "E41.filletArc", {"start": v(0, 25.08) * mm, "mid": v(-0.04, 25.42) * mm, "end": v(-0.14, 25.74) * mm});
            skPoint(sketch, "E42.visualSharp", {"position": v(-3.1, 28.4) * mm});
            skArc(sketch, "E42.filletArc", {"start": v(-2.95, 28.44) * mm, "mid": v(-3.1, 28.38) * mm, "end": v(-3.22, 28.3) * mm});
            skPoint(sketch, "E43.visualSharp", {"position": v(-2.5, 28.47) * mm});
            skArc(sketch, "E43.filletArc", {"start": v(-2.37, 28.38) * mm, "mid": v(-2.5, 28.44) * mm, "end": v(-2.65, 28.47) * mm});
            skArc(sketch, "E44.1.0", {"start": v(-13.55, 17.62) * mm, "mid": v(-12.95, 18.62) * mm, "end": v(-13.2, 19.76) * mm});
            skArc(sketch, "E44.1.1", {"start": v(-9.1, 21.95) * mm, "mid": v(-8.28, 21.11) * mm, "end": v(-7.12, 21.05) * mm});
            skPoint(sketch, "E44.1.2", {"position": v(-13.74, 25.06) * mm});
            skPoint(sketch, "E44.1.3", {"position": v(-14.11, 21.12) * mm});
            skPoint(sketch, "E44.1.4", {"position": v(-9.72, 23.47) * mm});
            skPoint(sketch, "E44.1.5", {"position": v(-13.2, 25.34) * mm});
            skLineSegment(sketch, "E44.1.6", {"start": v(-9.6, 23.17) * mm, "end": v(-9.1, 21.95) * mm});
            skArc(sketch, "E44.1.7", {"start": v(-9.98, 23.72) * mm, "mid": v(-11.4, 24.73) * mm, "end": v(-13.05, 25.31) * mm});
            skArc(sketch, "E44.1.8", {"start": v(-14.18, 21.48) * mm, "mid": v(-14.23, 23.22) * mm, "end": v(-13.8, 24.9) * mm});
            skLineSegment(sketch, "E44.1.9", {"start": v(-13.94, 20.86) * mm, "end": v(-13.2, 19.76) * mm});
            skArc(sketch, "E44.1.10", {"start": v(-9.6, 23.17) * mm, "mid": v(-9.76, 23.47) * mm, "end": v(-9.98, 23.72) * mm});
            skArc(sketch, "E44.1.11", {"start": v(-14.18, 21.48) * mm, "mid": v(-14.1, 21.15) * mm, "end": v(-13.94, 20.86) * mm});
            skArc(sketch, "E44.1.12", {"start": v(-13.05, 25.31) * mm, "mid": v(-13.2, 25.32) * mm, "end": v(-13.34, 25.28) * mm});
            skLineSegment(sketch, "E44.1.13", {"start": v(-13.61, 25.14) * mm, "end": v(-13.48, 25.23) * mm});
            skLineSegment(sketch, "E44.1.14", {"start": v(-13.34, 25.28) * mm, "end": v(-13.48, 25.23) * mm});
            skArc(sketch, "E44.1.15", {"start": v(-13.61, 25.14) * mm, "mid": v(-13.72, 25.04) * mm, "end": v(-13.8, 24.9) * mm});
            skArc(sketch, "E44.2.0", {"start": v(-19.26, 11.09) * mm, "mid": v(-19.1, 12.24) * mm, "end": v(-19.76, 13.2) * mm});
            skArc(sketch, "E44.2.1", {"start": v(-16.8, 16.8) * mm, "mid": v(-15.73, 16.34) * mm, "end": v(-14.63, 16.73) * mm});
            skPoint(sketch, "E44.2.2", {"position": v(-22.28, 17.9) * mm});
            skPoint(sketch, "E44.2.3", {"position": v(-21.12, 14.11) * mm});
            skPoint(sketch, "E44.2.4", {"position": v(-17.96, 17.96) * mm});
            skPoint(sketch, "E44.2.5", {"position": v(-21.9, 18.36) * mm});
            skLineSegment(sketch, "E44.2.6", {"start": v(-17.74, 17.74) * mm, "end": v(-16.8, 16.8) * mm});
            skArc(sketch, "E44.2.7", {"start": v(-18.3, 18.1) * mm, "mid": v(-20, 18.48) * mm, "end": v(-21.74, 18.4) * mm});
            skArc(sketch, "E44.2.8", {"start": v(-21.32, 14.42) * mm, "mid": v(-22.03, 16) * mm, "end": v(-22.28, 17.73) * mm});
            skLineSegment(sketch, "E44.2.9", {"start": v(-20.86, 13.94) * mm, "end": v(-19.76, 13.2) * mm});
            skArc(sketch, "E44.2.10", {"start": v(-17.74, 17.74) * mm, "mid": v(-18, 17.95) * mm, "end": v(-18.3, 18.1) * mm});
            skArc(sketch, "E44.2.11", {"start": v(-21.32, 14.42) * mm, "mid": v(-21.11, 14.15) * mm, "end": v(-20.86, 13.94) * mm});
            skArc(sketch, "E44.2.12", {"start": v(-21.74, 18.4) * mm, "mid": v(-21.88, 18.34) * mm, "end": v(-22, 18.25) * mm});
            skLineSegment(sketch, "E44.2.13", {"start": v(-22.2, 18.02) * mm, "end": v(-22.11, 18.15) * mm});
            skLineSegment(sketch, "E44.2.14", {"start": v(-22, 18.25) * mm, "end": v(-22.11, 18.15) * mm});
            skArc(sketch, "E44.2.15", {"start": v(-22.2, 18.02) * mm, "mid": v(-22.26, 17.88) * mm, "end": v(-22.28, 17.73) * mm});
            skArc(sketch, "E45.2.3.0", {"start": v(-22.04, 2.87) * mm, "mid": v(-22.32, 4) * mm, "end": v(-23.3, 4.64) * mm});
            skArc(sketch, "E45.4.3.0", {"start": v(-21.95, 9.1) * mm, "mid": v(-20.79, 9.07) * mm, "end": v(-19.92, 9.86) * mm});
            skPoint(sketch, "E45.8.3.0", {"position": v(-27.43, 8) * mm});
            skPoint(sketch, "E45.9.3.0", {"position": v(-24.91, 4.96) * mm});
            skPoint(sketch, "E45.10.3.0", {"position": v(-23.47, 9.72) * mm});
            skPoint(sketch, "E45.11.3.0", {"position": v(-27.25, 8.59) * mm});
            skLineSegment(sketch, "E45.12.3.0", {"start": v(-23.17, 9.6) * mm, "end": v(-21.95, 9.1) * mm});
            skArc(sketch, "E45.15.3.0", {"start": v(-23.83, 9.72) * mm, "mid": v(-25.55, 9.42) * mm, "end": v(-27.12, 8.67) * mm});
            skArc(sketch, "E45.19.3.0", {"start": v(-25.22, 5.16) * mm, "mid": v(-26.48, 6.36) * mm, "end": v(-27.37, 7.86) * mm});
            skLineSegment(sketch, "E45.23.3.0", {"start": v(-24.6, 4.9) * mm, "end": v(-23.3, 4.64) * mm});
            skArc(sketch, "E45.26.3.0", {"start": v(-23.17, 9.6) * mm, "mid": v(-23.5, 9.7) * mm, "end": v(-23.83, 9.72) * mm});
            skArc(sketch, "E45.30.3.0", {"start": v(-25.22, 5.16) * mm, "mid": v(-24.92, 5) * mm, "end": v(-24.6, 4.9) * mm});
            skArc(sketch, "E45.34.3.0", {"start": v(-27.12, 8.67) * mm, "mid": v(-27.24, 8.57) * mm, "end": v(-27.31, 8.44) * mm});
            skLineSegment(sketch, "E45.38.3.0", {"start": v(-27.4, 8.15) * mm, "end": v(-27.37, 8.3) * mm});
            skLineSegment(sketch, "E45.41.3.0", {"start": v(-27.31, 8.44) * mm, "end": v(-27.37, 8.3) * mm});
            skArc(sketch, "E45.44.3.0", {"start": v(-27.4, 8.15) * mm, "mid": v(-27.4, 8) * mm, "end": v(-27.37, 7.86) * mm});
            skArc(sketch, "E45.2.4.0", {"start": v(-21.46, -5.78) * mm, "mid": v(-22.16, -4.84) * mm, "end": v(-23.3, -4.64) * mm});
            skArc(sketch, "E45.4.4.0", {"start": v(-23.76, 0) * mm, "mid": v(-22.68, 0.43) * mm, "end": v(-22.18, 1.48) * mm});
            skPoint(sketch, "E45.8.4.0", {"position": v(-28.4, -3.1) * mm});
            skPoint(sketch, "E45.9.4.0", {"position": v(-24.91, -4.96) * mm});
            skPoint(sketch, "E45.10.4.0", {"position": v(-25.4, 0) * mm});
            skPoint(sketch, "E45.11.4.0", {"position": v(-28.47, -2.5) * mm});
            skLineSegment(sketch, "E45.12.4.0", {"start": v(-25.08, 0) * mm, "end": v(-23.76, 0) * mm});
            skArc(sketch, "E45.15.4.0", {"start": v(-25.74, -0.14) * mm, "mid": v(-27.21, -1.07) * mm, "end": v(-28.38, -2.37) * mm});
            skArc(sketch, "E45.19.4.0", {"start": v(-25.27, -4.88) * mm, "mid": v(-26.9, -4.26) * mm, "end": v(-28.3, -3.22) * mm});
            skLineSegment(sketch, "E45.23.4.0", {"start": v(-24.6, -4.9) * mm, "end": v(-23.3, -4.64) * mm});
            skArc(sketch, "E45.26.4.0", {"start": v(-25.08, 0) * mm, "mid": v(-25.42, -0.04) * mm, "end": v(-25.74, -0.14) * mm});
            skArc(sketch, "E45.30.4.0", {"start": v(-25.27, -4.88) * mm, "mid": v(-24.94, -4.92) * mm, "end": v(-24.6, -4.9) * mm});
            skArc(sketch, "E45.34.4.0", {"start": v(-28.38, -2.37) * mm, "mid": v(-28.44, -2.5) * mm, "end": v(-28.47, -2.65) * mm});
            skLineSegment(sketch, "E45.38.4.0", {"start": v(-28.44, -2.95) * mm, "end": v(-28.47, -2.8) * mm});
            skLineSegment(sketch, "E45.41.4.0", {"start": v(-28.47, -2.65) * mm, "end": v(-28.47, -2.8) * mm});
            skArc(sketch, "E45.44.4.0", {"start": v(-28.44, -2.95) * mm, "mid": v(-28.38, -3.1) * mm, "end": v(-28.3, -3.22) * mm});
            skArc(sketch, "E45.2.5.0", {"start": v(-17.62, -13.55) * mm, "mid": v(-18.62, -12.95) * mm, "end": v(-19.76, -13.2) * mm});
            skArc(sketch, "E45.4.5.0", {"start": v(-21.95, -9.1) * mm, "mid": v(-21.11, -8.28) * mm, "end": v(-21.05, -7.12) * mm});
            skPoint(sketch, "E45.8.5.0", {"position": v(-25.06, -13.74) * mm});
            skPoint(sketch, "E45.9.5.0", {"position": v(-21.12, -14.11) * mm});
            skPoint(sketch, "E45.10.5.0", {"position": v(-23.47, -9.72) * mm});
            skPoint(sketch, "E45.11.5.0", {"position": v(-25.34, -13.2) * mm});
            skLineSegment(sketch, "E45.12.5.0", {"start": v(-23.17, -9.6) * mm, "end": v(-21.95, -9.1) * mm});
            skArc(sketch, "E45.15.5.0", {"start": v(-23.72, -9.98) * mm, "mid": v(-24.73, -11.4) * mm, "end": v(-25.31, -13.05) * mm});
            skArc(sketch, "E45.19.5.0", {"start": v(-21.48, -14.18) * mm, "mid": v(-23.22, -14.23) * mm, "end": v(-24.9, -13.8) * mm});
            skLineSegment(sketch, "E45.23.5.0", {"start": v(-20.86, -13.94) * mm, "end": v(-19.76, -13.2) * mm});
            skArc(sketch, "E45.26.5.0", {"start": v(-23.17, -9.6) * mm, "mid": v(-23.47, -9.76) * mm, "end": v(-23.72, -9.98) * mm});
            skArc(sketch, "E45.30.5.0", {"start": v(-21.48, -14.18) * mm, "mid": v(-21.15, -14.1) * mm, "end": v(-20.86, -13.94) * mm});
            skArc(sketch, "E45.34.5.0", {"start": v(-25.31, -13.05) * mm, "mid": v(-25.32, -13.2) * mm, "end": v(-25.28, -13.34) * mm});
            skLineSegment(sketch, "E45.38.5.0", {"start": v(-25.14, -13.61) * mm, "end": v(-25.23, -13.48) * mm});
            skLineSegment(sketch, "E45.41.5.0", {"start": v(-25.28, -13.34) * mm, "end": v(-25.23, -13.48) * mm});
            skArc(sketch, "E45.44.5.0", {"start": v(-25.14, -13.61) * mm, "mid": v(-25.04, -13.72) * mm, "end": v(-24.9, -13.8) * mm});
            skArc(sketch, "E45.2.6.0", {"start": v(-11.09, -19.26) * mm, "mid": v(-12.24, -19.1) * mm, "end": v(-13.2, -19.76) * mm});
            skArc(sketch, "E45.4.6.0", {"start": v(-16.8, -16.8) * mm, "mid": v(-16.34, -15.73) * mm, "end": v(-16.73, -14.63) * mm});
            skPoint(sketch, "E45.8.6.0", {"position": v(-17.9, -22.28) * mm});
            skPoint(sketch, "E45.9.6.0", {"position": v(-14.11, -21.12) * mm});
            skPoint(sketch, "E45.10.6.0", {"position": v(-17.96, -17.96) * mm});
            skPoint(sketch, "E45.11.6.0", {"position": v(-18.36, -21.9) * mm});
            skLineSegment(sketch, "E45.12.6.0", {"start": v(-17.74, -17.74) * mm, "end": v(-16.8, -16.8) * mm});
            skArc(sketch, "E45.15.6.0", {"start": v(-18.1, -18.3) * mm, "mid": v(-18.48, -20) * mm, "end": v(-18.4, -21.74) * mm});
            skArc(sketch, "E45.19.6.0", {"start": v(-14.42, -21.32) * mm, "mid": v(-16, -22.03) * mm, "end": v(-17.73, -22.28) * mm});
            skLineSegment(sketch, "E45.23.6.0", {"start": v(-13.94, -20.86) * mm, "end": v(-13.2, -19.76) * mm});
            skArc(sketch, "E45.26.6.0", {"start": v(-17.74, -17.74) * mm, "mid": v(-17.95, -18) * mm, "end": v(-18.1, -18.3) * mm});
            skArc(sketch, "E45.30.6.0", {"start": v(-14.42, -21.32) * mm, "mid": v(-14.15, -21.11) * mm, "end": v(-13.94, -20.86) * mm});
            skArc(sketch, "E45.34.6.0", {"start": v(-18.4, -21.74) * mm, "mid": v(-18.34, -21.88) * mm, "end": v(-18.25, -22) * mm});
            skLineSegment(sketch, "E45.38.6.0", {"start": v(-18.02, -22.2) * mm, "end": v(-18.15, -22.11) * mm});
            skLineSegment(sketch, "E45.41.6.0", {"start": v(-18.25, -22) * mm, "end": v(-18.15, -22.11) * mm});
            skArc(sketch, "E45.44.6.0", {"start": v(-18.02, -22.2) * mm, "mid": v(-17.88, -22.26) * mm, "end": v(-17.73, -22.28) * mm});
            skArc(sketch, "E45.2.7.0", {"start": v(-2.87, -22.04) * mm, "mid": v(-4, -22.32) * mm, "end": v(-4.64, -23.3) * mm});
            skArc(sketch, "E45.4.7.0", {"start": v(-9.1, -21.95) * mm, "mid": v(-9.07, -20.79) * mm, "end": v(-9.86, -19.92) * mm});
            skPoint(sketch, "E45.8.7.0", {"position": v(-8, -27.43) * mm});
            skPoint(sketch, "E45.9.7.0", {"position": v(-4.96, -24.91) * mm});
            skPoint(sketch, "E45.10.7.0", {"position": v(-9.72, -23.47) * mm});
            skPoint(sketch, "E45.11.7.0", {"position": v(-8.59, -27.25) * mm});
            skLineSegment(sketch, "E45.12.7.0", {"start": v(-9.6, -23.17) * mm, "end": v(-9.1, -21.95) * mm});
            skArc(sketch, "E45.15.7.0", {"start": v(-9.72, -23.83) * mm, "mid": v(-9.42, -25.55) * mm, "end": v(-8.67, -27.12) * mm});
            skArc(sketch, "E45.19.7.0", {"start": v(-5.16, -25.22) * mm, "mid": v(-6.36, -26.48) * mm, "end": v(-7.86, -27.37) * mm});
            skLineSegment(sketch, "E45.23.7.0", {"start": v(-4.9, -24.6) * mm, "end": v(-4.64, -23.3) * mm});
            skArc(sketch, "E45.26.7.0", {"start": v(-9.6, -23.17) * mm, "mid": v(-9.7, -23.5) * mm, "end": v(-9.72, -23.83) * mm});
            skArc(sketch, "E45.30.7.0", {"start": v(-5.16, -25.22) * mm, "mid": v(-5, -24.92) * mm, "end": v(-4.9, -24.6) * mm});
            skArc(sketch, "E45.34.7.0", {"start": v(-8.67, -27.12) * mm, "mid": v(-8.57, -27.24) * mm, "end": v(-8.44, -27.31) * mm});
            skLineSegment(sketch, "E45.38.7.0", {"start": v(-8.15, -27.4) * mm, "end": v(-8.3, -27.37) * mm});
            skLineSegment(sketch, "E45.41.7.0", {"start": v(-8.44, -27.31) * mm, "end": v(-8.3, -27.37) * mm});
            skArc(sketch, "E45.44.7.0", {"start": v(-8.15, -27.4) * mm, "mid": v(-8, -27.4) * mm, "end": v(-7.86, -27.37) * mm});
            skArc(sketch, "E45.2.8.0", {"start": v(5.78, -21.46) * mm, "mid": v(4.84, -22.16) * mm, "end": v(4.64, -23.3) * mm});
            skArc(sketch, "E45.4.8.0", {"start": v(0, -23.76) * mm, "mid": v(-0.43, -22.68) * mm, "end": v(-1.48, -22.18) * mm});
            skPoint(sketch, "E45.8.8.0", {"position": v(3.1, -28.4) * mm});
            skPoint(sketch, "E45.9.8.0", {"position": v(4.96, -24.91) * mm});
            skPoint(sketch, "E45.10.8.0", {"position": v(0, -25.4) * mm});
            skPoint(sketch, "E45.11.8.0", {"position": v(2.5, -28.47) * mm});
            skLineSegment(sketch, "E45.12.8.0", {"start": v(0, -25.08) * mm, "end": v(0, -23.76) * mm});
            skArc(sketch, "E45.15.8.0", {"start": v(0.14, -25.74) * mm, "mid": v(1.07, -27.21) * mm, "end": v(2.37, -28.38) * mm});
            skArc(sketch, "E45.19.8.0", {"start": v(4.88, -25.27) * mm, "mid": v(4.26, -26.9) * mm, "end": v(3.22, -28.3) * mm});
            skLineSegment(sketch, "E45.23.8.0", {"start": v(4.9, -24.6) * mm, "end": v(4.64, -23.3) * mm});
            skArc(sketch, "E45.26.8.0", {"start": v(0, -25.08) * mm, "mid": v(0.04, -25.42) * mm, "end": v(0.14, -25.74) * mm});
            skArc(sketch, "E45.30.8.0", {"start": v(4.88, -25.27) * mm, "mid": v(4.92, -24.94) * mm, "end": v(4.9, -24.6) * mm});
            skArc(sketch, "E45.34.8.0", {"start": v(2.37, -28.38) * mm, "mid": v(2.5, -28.44) * mm, "end": v(2.65, -28.47) * mm});
            skLineSegment(sketch, "E45.38.8.0", {"start": v(2.95, -28.44) * mm, "end": v(2.8, -28.47) * mm});
            skLineSegment(sketch, "E45.41.8.0", {"start": v(2.65, -28.47) * mm, "end": v(2.8, -28.47) * mm});
            skArc(sketch, "E45.44.8.0", {"start": v(2.95, -28.44) * mm, "mid": v(3.1, -28.38) * mm, "end": v(3.22, -28.3) * mm});
            skArc(sketch, "E45.2.9.0", {"start": v(13.55, -17.62) * mm, "mid": v(12.95, -18.62) * mm, "end": v(13.2, -19.76) * mm});
            skArc(sketch, "E45.4.9.0", {"start": v(9.1, -21.95) * mm, "mid": v(8.28, -21.11) * mm, "end": v(7.12, -21.05) * mm});
            skPoint(sketch, "E45.8.9.0", {"position": v(13.74, -25.06) * mm});
            skPoint(sketch, "E45.9.9.0", {"position": v(14.11, -21.12) * mm});
            skPoint(sketch, "E45.10.9.0", {"position": v(9.72, -23.47) * mm});
            skPoint(sketch, "E45.11.9.0", {"position": v(13.2, -25.34) * mm});
            skLineSegment(sketch, "E45.12.9.0", {"start": v(9.6, -23.17) * mm, "end": v(9.1, -21.95) * mm});
            skArc(sketch, "E45.15.9.0", {"start": v(9.98, -23.72) * mm, "mid": v(11.4, -24.73) * mm, "end": v(13.05, -25.31) * mm});
            skArc(sketch, "E45.19.9.0", {"start": v(14.18, -21.48) * mm, "mid": v(14.23, -23.22) * mm, "end": v(13.8, -24.9) * mm});
            skLineSegment(sketch, "E45.23.9.0", {"start": v(13.94, -20.86) * mm, "end": v(13.2, -19.76) * mm});
            skArc(sketch, "E45.26.9.0", {"start": v(9.6, -23.17) * mm, "mid": v(9.76, -23.47) * mm, "end": v(9.98, -23.72) * mm});
            skArc(sketch, "E45.30.9.0", {"start": v(14.18, -21.48) * mm, "mid": v(14.1, -21.15) * mm, "end": v(13.94, -20.86) * mm});
            skArc(sketch, "E45.34.9.0", {"start": v(13.05, -25.31) * mm, "mid": v(13.2, -25.32) * mm, "end": v(13.34, -25.28) * mm});
            skLineSegment(sketch, "E45.38.9.0", {"start": v(13.61, -25.14) * mm, "end": v(13.48, -25.23) * mm});
            skLineSegment(sketch, "E45.41.9.0", {"start": v(13.34, -25.28) * mm, "end": v(13.48, -25.23) * mm});
            skArc(sketch, "E45.44.9.0", {"start": v(13.61, -25.14) * mm, "mid": v(13.72, -25.04) * mm, "end": v(13.8, -24.9) * mm});
            skArc(sketch, "E45.2.10.0", {"start": v(19.26, -11.09) * mm, "mid": v(19.1, -12.24) * mm, "end": v(19.76, -13.2) * mm});
            skArc(sketch, "E45.4.10.0", {"start": v(16.8, -16.8) * mm, "mid": v(15.73, -16.34) * mm, "end": v(14.63, -16.73) * mm});
            skPoint(sketch, "E45.8.10.0", {"position": v(22.28, -17.9) * mm});
            skPoint(sketch, "E45.9.10.0", {"position": v(21.12, -14.11) * mm});
            skPoint(sketch, "E45.10.10.0", {"position": v(17.96, -17.96) * mm});
            skPoint(sketch, "E45.11.10.0", {"position": v(21.9, -18.36) * mm});
            skLineSegment(sketch, "E45.12.10.0", {"start": v(17.74, -17.74) * mm, "end": v(16.8, -16.8) * mm});
            skArc(sketch, "E45.15.10.0", {"start": v(18.3, -18.1) * mm, "mid": v(20, -18.48) * mm, "end": v(21.74, -18.4) * mm});
            skArc(sketch, "E45.19.10.0", {"start": v(21.32, -14.42) * mm, "mid": v(22.03, -16) * mm, "end": v(22.28, -17.73) * mm});
            skLineSegment(sketch, "E45.23.10.0", {"start": v(20.86, -13.94) * mm, "end": v(19.76, -13.2) * mm});
            skArc(sketch, "E45.26.10.0", {"start": v(17.74, -17.74) * mm, "mid": v(18, -17.95) * mm, "end": v(18.3, -18.1) * mm});
            skArc(sketch, "E45.30.10.0", {"start": v(21.32, -14.42) * mm, "mid": v(21.11, -14.15) * mm, "end": v(20.86, -13.94) * mm});
            skArc(sketch, "E45.34.10.0", {"start": v(21.74, -18.4) * mm, "mid": v(21.88, -18.34) * mm, "end": v(22, -18.25) * mm});
            skLineSegment(sketch, "E45.38.10.0", {"start": v(22.2, -18.02) * mm, "end": v(22.11, -18.15) * mm});
            skLineSegment(sketch, "E45.41.10.0", {"start": v(22, -18.25) * mm, "end": v(22.11, -18.15) * mm});
            skArc(sketch, "E45.44.10.0", {"start": v(22.2, -18.02) * mm, "mid": v(22.26, -17.88) * mm, "end": v(22.28, -17.73) * mm});
            skArc(sketch, "E45.2.11.0", {"start": v(22.04, -2.87) * mm, "mid": v(22.32, -4) * mm, "end": v(23.3, -4.64) * mm});
            skArc(sketch, "E45.4.11.0", {"start": v(21.95, -9.1) * mm, "mid": v(20.79, -9.07) * mm, "end": v(19.92, -9.86) * mm});
            skPoint(sketch, "E45.8.11.0", {"position": v(27.43, -8) * mm});
            skPoint(sketch, "E45.9.11.0", {"position": v(24.91, -4.96) * mm});
            skPoint(sketch, "E45.10.11.0", {"position": v(23.47, -9.72) * mm});
            skPoint(sketch, "E45.11.11.0", {"position": v(27.25, -8.59) * mm});
            skLineSegment(sketch, "E45.12.11.0", {"start": v(23.17, -9.6) * mm, "end": v(21.95, -9.1) * mm});
            skArc(sketch, "E45.15.11.0", {"start": v(23.83, -9.72) * mm, "mid": v(25.55, -9.42) * mm, "end": v(27.12, -8.67) * mm});
            skArc(sketch, "E45.19.11.0", {"start": v(25.22, -5.16) * mm, "mid": v(26.48, -6.36) * mm, "end": v(27.37, -7.86) * mm});
            skLineSegment(sketch, "E45.23.11.0", {"start": v(24.6, -4.9) * mm, "end": v(23.3, -4.64) * mm});
            skArc(sketch, "E45.26.11.0", {"start": v(23.17, -9.6) * mm, "mid": v(23.5, -9.7) * mm, "end": v(23.83, -9.72) * mm});
            skArc(sketch, "E45.30.11.0", {"start": v(25.22, -5.16) * mm, "mid": v(24.92, -5) * mm, "end": v(24.6, -4.9) * mm});
            skArc(sketch, "E45.34.11.0", {"start": v(27.12, -8.67) * mm, "mid": v(27.24, -8.57) * mm, "end": v(27.31, -8.44) * mm});
            skLineSegment(sketch, "E45.38.11.0", {"start": v(27.4, -8.15) * mm, "end": v(27.37, -8.3) * mm});
            skLineSegment(sketch, "E45.41.11.0", {"start": v(27.31, -8.44) * mm, "end": v(27.37, -8.3) * mm});
            skArc(sketch, "E45.44.11.0", {"start": v(27.4, -8.15) * mm, "mid": v(27.4, -8) * mm, "end": v(27.37, -7.86) * mm});
            skArc(sketch, "E45.2.12.0", {"start": v(21.46, 5.78) * mm, "mid": v(22.16, 4.84) * mm, "end": v(23.3, 4.64) * mm});
            skArc(sketch, "E45.4.12.0", {"start": v(23.76, 0) * mm, "mid": v(22.68, -0.43) * mm, "end": v(22.18, -1.48) * mm});
            skPoint(sketch, "E45.8.12.0", {"position": v(28.4, 3.1) * mm});
            skPoint(sketch, "E45.9.12.0", {"position": v(24.91, 4.96) * mm});
            skPoint(sketch, "E45.10.12.0", {"position": v(25.4, 0) * mm});
            skPoint(sketch, "E45.11.12.0", {"position": v(28.47, 2.5) * mm});
            skLineSegment(sketch, "E45.12.12.0", {"start": v(25.08, 0) * mm, "end": v(23.76, 0) * mm});
            skArc(sketch, "E45.15.12.0", {"start": v(25.74, 0.14) * mm, "mid": v(27.21, 1.07) * mm, "end": v(28.38, 2.37) * mm});
            skArc(sketch, "E45.19.12.0", {"start": v(25.27, 4.88) * mm, "mid": v(26.9, 4.26) * mm, "end": v(28.3, 3.22) * mm});
            skLineSegment(sketch, "E45.23.12.0", {"start": v(24.6, 4.9) * mm, "end": v(23.3, 4.64) * mm});
            skArc(sketch, "E45.26.12.0", {"start": v(25.08, 0) * mm, "mid": v(25.42, 0.04) * mm, "end": v(25.74, 0.14) * mm});
            skArc(sketch, "E45.30.12.0", {"start": v(25.27, 4.88) * mm, "mid": v(24.94, 4.92) * mm, "end": v(24.6, 4.9) * mm});
            skArc(sketch, "E45.34.12.0", {"start": v(28.38, 2.37) * mm, "mid": v(28.44, 2.5) * mm, "end": v(28.47, 2.65) * mm});
            skLineSegment(sketch, "E45.38.12.0", {"start": v(28.44, 2.95) * mm, "end": v(28.47, 2.8) * mm});
            skLineSegment(sketch, "E45.41.12.0", {"start": v(28.47, 2.65) * mm, "end": v(28.47, 2.8) * mm});
            skArc(sketch, "E45.44.12.0", {"start": v(28.44, 2.95) * mm, "mid": v(28.38, 3.1) * mm, "end": v(28.3, 3.22) * mm});
            skArc(sketch, "E45.2.13.0", {"start": v(17.62, 13.55) * mm, "mid": v(18.62, 12.95) * mm, "end": v(19.76, 13.2) * mm});
            skArc(sketch, "E45.4.13.0", {"start": v(21.95, 9.1) * mm, "mid": v(21.11, 8.28) * mm, "end": v(21.05, 7.12) * mm});
            skPoint(sketch, "E45.8.13.0", {"position": v(25.06, 13.74) * mm});
            skPoint(sketch, "E45.9.13.0", {"position": v(21.12, 14.11) * mm});
            skPoint(sketch, "E45.10.13.0", {"position": v(23.47, 9.72) * mm});
            skPoint(sketch, "E45.11.13.0", {"position": v(25.34, 13.2) * mm});
            skLineSegment(sketch, "E45.12.13.0", {"start": v(23.17, 9.6) * mm, "end": v(21.95, 9.1) * mm});
            skArc(sketch, "E45.15.13.0", {"start": v(23.72, 9.98) * mm, "mid": v(24.73, 11.4) * mm, "end": v(25.31, 13.05) * mm});
            skArc(sketch, "E45.19.13.0", {"start": v(21.48, 14.18) * mm, "mid": v(23.22, 14.23) * mm, "end": v(24.9, 13.8) * mm});
            skLineSegment(sketch, "E45.23.13.0", {"start": v(20.86, 13.94) * mm, "end": v(19.76, 13.2) * mm});
            skArc(sketch, "E45.26.13.0", {"start": v(23.17, 9.6) * mm, "mid": v(23.47, 9.76) * mm, "end": v(23.72, 9.98) * mm});
            skArc(sketch, "E45.30.13.0", {"start": v(21.48, 14.18) * mm, "mid": v(21.15, 14.1) * mm, "end": v(20.86, 13.94) * mm});
            skArc(sketch, "E45.34.13.0", {"start": v(25.31, 13.05) * mm, "mid": v(25.32, 13.2) * mm, "end": v(25.28, 13.34) * mm});
            skLineSegment(sketch, "E45.38.13.0", {"start": v(25.14, 13.61) * mm, "end": v(25.23, 13.48) * mm});
            skLineSegment(sketch, "E45.41.13.0", {"start": v(25.28, 13.34) * mm, "end": v(25.23, 13.48) * mm});
            skArc(sketch, "E45.44.13.0", {"start": v(25.14, 13.61) * mm, "mid": v(25.04, 13.72) * mm, "end": v(24.9, 13.8) * mm});
            skArc(sketch, "E45.2.14.0", {"start": v(11.09, 19.26) * mm, "mid": v(12.24, 19.1) * mm, "end": v(13.2, 19.76) * mm});
            skArc(sketch, "E45.4.14.0", {"start": v(16.8, 16.8) * mm, "mid": v(16.34, 15.73) * mm, "end": v(16.73, 14.63) * mm});
            skPoint(sketch, "E45.8.14.0", {"position": v(17.9, 22.28) * mm});
            skPoint(sketch, "E45.9.14.0", {"position": v(14.11, 21.12) * mm});
            skPoint(sketch, "E45.10.14.0", {"position": v(17.96, 17.96) * mm});
            skPoint(sketch, "E45.11.14.0", {"position": v(18.36, 21.9) * mm});
            skLineSegment(sketch, "E45.12.14.0", {"start": v(17.74, 17.74) * mm, "end": v(16.8, 16.8) * mm});
            skArc(sketch, "E45.15.14.0", {"start": v(18.1, 18.3) * mm, "mid": v(18.48, 20) * mm, "end": v(18.4, 21.74) * mm});
            skArc(sketch, "E45.19.14.0", {"start": v(14.42, 21.32) * mm, "mid": v(16, 22.03) * mm, "end": v(17.73, 22.28) * mm});
            skLineSegment(sketch, "E45.23.14.0", {"start": v(13.94, 20.86) * mm, "end": v(13.2, 19.76) * mm});
            skArc(sketch, "E45.26.14.0", {"start": v(17.74, 17.74) * mm, "mid": v(17.95, 18) * mm, "end": v(18.1, 18.3) * mm});
            skArc(sketch, "E45.30.14.0", {"start": v(14.42, 21.32) * mm, "mid": v(14.15, 21.11) * mm, "end": v(13.94, 20.86) * mm});
            skArc(sketch, "E45.34.14.0", {"start": v(18.4, 21.74) * mm, "mid": v(18.34, 21.88) * mm, "end": v(18.25, 22) * mm});
            skLineSegment(sketch, "E45.38.14.0", {"start": v(18.02, 22.2) * mm, "end": v(18.15, 22.11) * mm});
            skLineSegment(sketch, "E45.41.14.0", {"start": v(18.25, 22) * mm, "end": v(18.15, 22.11) * mm});
            skArc(sketch, "E45.44.14.0", {"start": v(18.02, 22.2) * mm, "mid": v(17.88, 22.26) * mm, "end": v(17.73, 22.28) * mm});
            skArc(sketch, "E45.2.15.0", {"start": v(2.87, 22.04) * mm, "mid": v(4, 22.32) * mm, "end": v(4.64, 23.3) * mm});
            skArc(sketch, "E45.4.15.0", {"start": v(9.1, 21.95) * mm, "mid": v(9.07, 20.79) * mm, "end": v(9.86, 19.92) * mm});
            skPoint(sketch, "E45.8.15.0", {"position": v(8, 27.43) * mm});
            skPoint(sketch, "E45.9.15.0", {"position": v(4.96, 24.91) * mm});
            skPoint(sketch, "E45.10.15.0", {"position": v(9.72, 23.47) * mm});
            skPoint(sketch, "E45.11.15.0", {"position": v(8.59, 27.25) * mm});
            skLineSegment(sketch, "E45.12.15.0", {"start": v(9.6, 23.17) * mm, "end": v(9.1, 21.95) * mm});
            skArc(sketch, "E45.15.15.0", {"start": v(9.72, 23.83) * mm, "mid": v(9.42, 25.55) * mm, "end": v(8.67, 27.12) * mm});
            skArc(sketch, "E45.19.15.0", {"start": v(5.16, 25.22) * mm, "mid": v(6.36, 26.48) * mm, "end": v(7.86, 27.37) * mm});
            skLineSegment(sketch, "E45.23.15.0", {"start": v(4.9, 24.6) * mm, "end": v(4.64, 23.3) * mm});
            skArc(sketch, "E45.26.15.0", {"start": v(9.6, 23.17) * mm, "mid": v(9.7, 23.5) * mm, "end": v(9.72, 23.83) * mm});
            skArc(sketch, "E45.30.15.0", {"start": v(5.16, 25.22) * mm, "mid": v(5, 24.92) * mm, "end": v(4.9, 24.6) * mm});
            skArc(sketch, "E45.34.15.0", {"start": v(8.67, 27.12) * mm, "mid": v(8.57, 27.24) * mm, "end": v(8.44, 27.31) * mm});
            skLineSegment(sketch, "E45.38.15.0", {"start": v(8.15, 27.4) * mm, "end": v(8.3, 27.37) * mm});
            skLineSegment(sketch, "E45.41.15.0", {"start": v(8.44, 27.31) * mm, "end": v(8.3, 27.37) * mm});
            skArc(sketch, "E45.44.15.0", {"start": v(8.15, 27.4) * mm, "mid": v(8, 27.4) * mm, "end": v(7.86, 27.37) * mm});
            skArc(sketch, "E46.trimOffspring", {"start": v(-13.55, 17.62) * mm, "mid": v(-14.1, 17.18) * mm, "end": v(-14.63, 16.73) * mm});
            skArc(sketch, "E47.trimOffspring", {"start": v(-19.26, 11.09) * mm, "mid": v(-19.6, 10.48) * mm, "end": v(-19.92, 9.86) * mm});
            skArc(sketch, "E48.trimOffspring", {"start": v(-22.04, 2.87) * mm, "mid": v(-22.12, 2.18) * mm, "end": v(-22.18, 1.48) * mm});
            skArc(sketch, "E49.trimOffspring", {"start": v(-21.46, -5.78) * mm, "mid": v(-21.27, -6.45) * mm, "end": v(-21.05, -7.12) * mm});
            skArc(sketch, "E50.trimOffspring", {"start": v(-17.62, -13.55) * mm, "mid": v(-17.18, -14.1) * mm, "end": v(-16.73, -14.63) * mm});
            skArc(sketch, "E51.trimOffspring", {"start": v(-11.09, -19.26) * mm, "mid": v(-10.48, -19.6) * mm, "end": v(-9.86, -19.92) * mm});
            skArc(sketch, "E52.trimOffspring", {"start": v(2.87, 22.04) * mm, "mid": v(2.18, 22.12) * mm, "end": v(1.48, 22.18) * mm});
            skArc(sketch, "E53.trimOffspring", {"start": v(11.09, 19.26) * mm, "mid": v(10.48, 19.6) * mm, "end": v(9.86, 19.92) * mm});
            skArc(sketch, "E54.trimOffspring", {"start": v(17.62, 13.55) * mm, "mid": v(17.18, 14.1) * mm, "end": v(16.73, 14.63) * mm});
            skArc(sketch, "E55.trimOffspring", {"start": v(21.46, 5.78) * mm, "mid": v(21.27, 6.45) * mm, "end": v(21.05, 7.12) * mm});
            skArc(sketch, "E56.trimOffspring", {"start": v(22.04, -2.87) * mm, "mid": v(22.12, -2.18) * mm, "end": v(22.18, -1.48) * mm});
            skArc(sketch, "E57.trimOffspring", {"start": v(19.26, -11.09) * mm, "mid": v(19.6, -10.48) * mm, "end": v(19.92, -9.86) * mm});
            skArc(sketch, "E58.trimOffspring", {"start": v(13.55, -17.62) * mm, "mid": v(14.1, -17.18) * mm, "end": v(14.63, -16.73) * mm});
            skArc(sketch, "E59.trimOffspring", {"start": v(5.78, -21.46) * mm, "mid": v(6.45, -21.27) * mm, "end": v(7.12, -21.05) * mm});
            skArc(sketch, "E60.trimOffspring", {"start": v(-2.87, -22.04) * mm, "mid": v(-2.18, -22.12) * mm, "end": v(-1.48, -22.18) * mm});
            skSolve(sketch);
        }
        {
            var Q0;
            Q0=makeQuery(id+"F0.imprint","IMPRINT",FACE,{"disambiguationData":[TD([[makeQuery(id+"F0.imprint","IMPRINT",EDGE,{"derivedFrom":sQuery(id+"F0.wireOp",EDGE,"E0")}),1.0]])]});
            var Q1;
            Q1=makeQuery(id+"F2.imprint","IMPRINT",FACE,{"disambiguationData":[TD([[makeQuery(id+"F2.imprint","IMPRINT",EDGE,{"derivedFrom":sQuery(id+"F2.wireOp",EDGE,"E30")}),1.0]])]});
            var Q2;
            Q2=sQuery(id+"F0.wireOp",VERTEX,"E14.47.15.0.end");
            var Q3;
            Q3=sQuery(id+"F2.wireOp",VERTEX,"E34.MirrorCS.end");
            loft(context, id + "F3", {"sheetProfilesArray" : [{ "sheetProfileEntities" : qUnion([Q0]) }, { "sheetProfileEntities" : qUnion([Q1]) }], "matchConnections" : true, "connections" : [{ "connectionEntities" : qUnion([Q2, Q3]), "connectionEdgeQueries" : qUnion([]), "connectionEdgeParameters" : [] }]});
        }
        {
            var Q0;
            Q0=sQuery(id+"F2.wireOp",VERTEX,"E30.center");
            var Q1;
            Q1=makeQuery(id+"F3.opLoft","SWEPT_BODY",BODY,{"disambiguationData":[OSD([makeQuery(id+"F0.imprint","IMPRINT",FACE,{"disambiguationData":[TD([[makeQuery(id+"F0.imprint","IMPRINT",EDGE,{"derivedFrom":sQuery(id+"F0.wireOp",EDGE,"E0")}),1.0]])]}),makeQuery(id+"F2.imprint","IMPRINT",FACE,{"disambiguationData":[TD([[makeQuery(id+"F2.imprint","IMPRINT",EDGE,{"derivedFrom":sQuery(id+"F2.wireOp",EDGE,"E30")}),1.0]])]})])]});
            hole(context, id + "F4", {"style" : HoleStyle.SIMPLE, "endStyle" : HoleEndStyle.THROUGH, "holeDiameter" : 12.7 * mm, "tappedDepth" : 12.7 * mm, "tapClearance" : 3, "locations" : qUnion([Q0]), "scope" : qUnion([Q1])});
        }
    });
